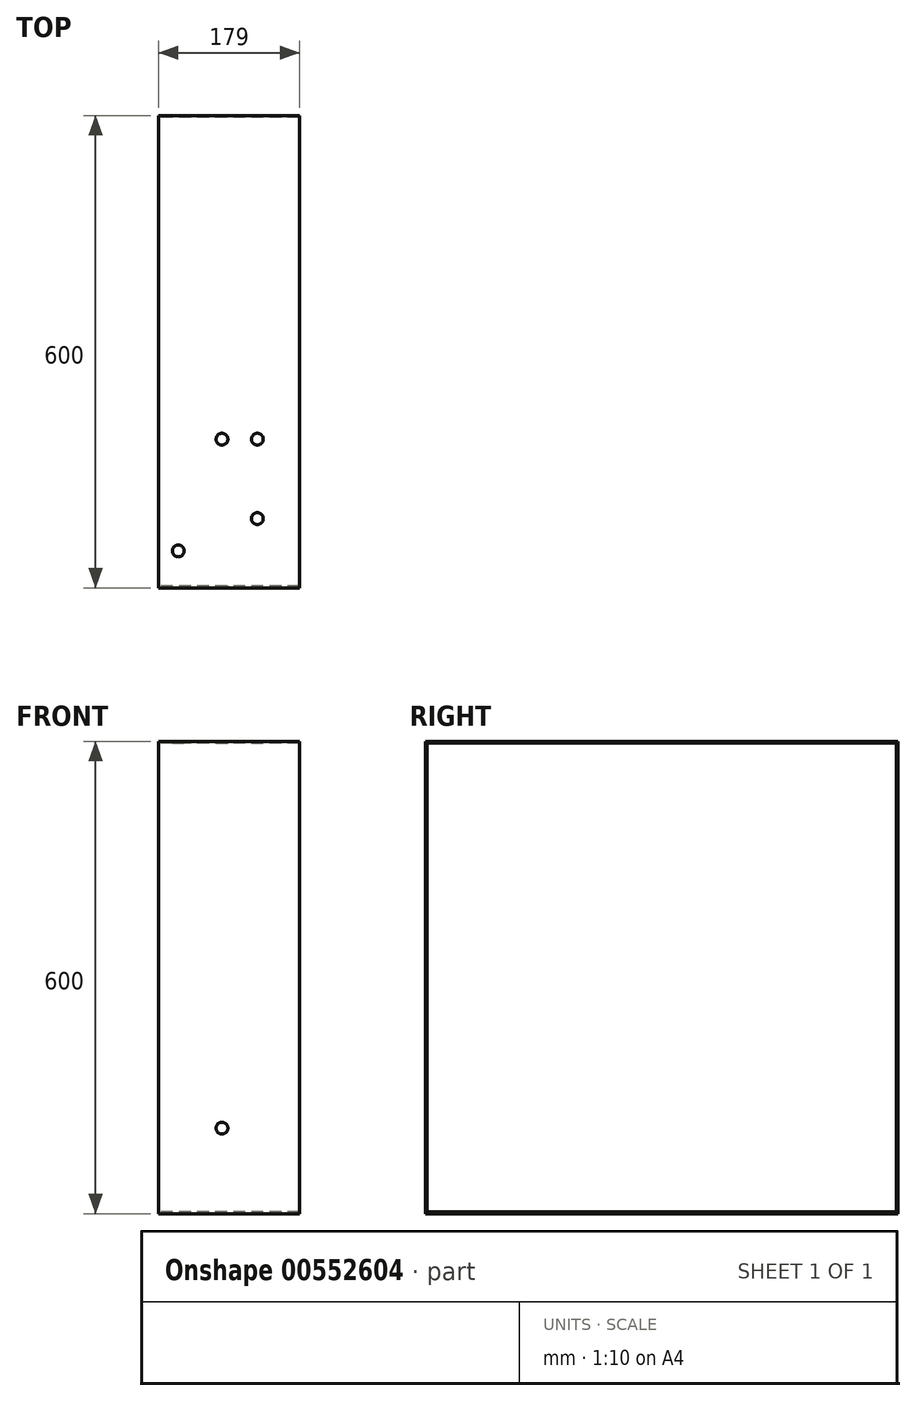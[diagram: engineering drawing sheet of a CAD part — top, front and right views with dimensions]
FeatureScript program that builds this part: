
annotation { "Feature Type Name" : "Feature", "Feature Type Description" : "" }
export const myFeature = defineFeature(function(context is Context, id is Id, definition is map)
    precondition{}
    {
        {
            var Q0;
            Q0=qCreatedBy(makeId("Right.planeOp"),FACE);
            var sketch = newSketch(context, id + "F0", { "sketchPlane" : qUnion([Q0])});
            skLineSegment(sketch, "E0", {"start": v(-190.86, -297.99) * mm, "end": v(405.14, -297.99) * mm});
            skLineSegment(sketch, "E1", {"start": v(-192.86, -299.99) * mm, "end": v(407.14, -299.99) * mm});
            skLineSegment(sketch, "E2", {"start": v(405.14, 298.01) * mm, "end": v(-190.86, 298.01) * mm});
            skLineSegment(sketch, "E3", {"start": v(407.14, 300.01) * mm, "end": v(-192.86, 300.01) * mm});
            skLineSegment(sketch, "E4", {"start": v(-192.86, 300.01) * mm, "end": v(-192.86, -299.99) * mm});
            skLineSegment(sketch, "E5", {"start": v(-190.86, 298.01) * mm, "end": v(-190.86, -297.99) * mm});
            skLineSegment(sketch, "E6", {"start": v(-139.36, -3.52) * mm, "end": v(-139.36, 3.48) * mm});
            skLineSegment(sketch, "E7", {"start": v(-146.36, 3.48) * mm, "end": v(-146.36, -3.52) * mm});
            skLineSegment(sketch, "E8", {"start": v(-139.36, 3.48) * mm, "end": v(-146.36, 3.48) * mm});
            skLineSegment(sketch, "E9", {"start": v(-146.36, -3.52) * mm, "end": v(-139.36, -3.52) * mm});
            skCircle(sketch, "E10", {"center": v(-142.86, -0.02) * mm, "radius": 16.5 * mm});
            skCircle(sketch, "E11", {"center": v(-142.86, -0.02) * mm, "radius": 8.5 * mm});
            skLineSegment(sketch, "E12", {"start": v(405.14, -297.99) * mm, "end": v(405.14, 298.01) * mm});
            skLineSegment(sketch, "E13", {"start": v(407.14, -299.99) * mm, "end": v(407.14, 300.01) * mm});
            skSolve(sketch);
        }
        {
            var Q0;
            Q0 = qSketchRegion(id + "F0", true);
            extrude(context, id + "F1", {"entities" : qUnion([Q0]), "depth" : 179 * mm, "offsetDistance" : 25 * mm});
        }
        {
            var Q0;
            Q0=makeQuery(id+"F1.opExtrude","SWEPT_FACE",FACE,{"disambiguationData":[OSD([sQuery(id+"F0.wireOp",EDGE,"E3")])]});
            var sketch = newSketch(context, id + "F2", { "sketchPlane" : qUnion([Q0])});
            skCircle(sketch, "E14", {"center": v(25, -145.96) * mm, "radius": 7.5 * mm});
            skCircle(sketch, "E15", {"center": v(80.5, -3.96) * mm, "radius": 7.5 * mm});
            skCircle(sketch, "E16", {"center": v(125.5, -3.96) * mm, "radius": 7.5 * mm});
            skCircle(sketch, "E17", {"center": v(125.5, -104.86) * mm, "radius": 7.5 * mm});
            skSolve(sketch);
        }
        {
            var Q0;
            Q0 = qSketchRegion(id + "F2", true);
            extrude(context, id + "F3", {"entities" : qUnion([Q0]), "operationType" : NewBodyOperationType.REMOVE, "oppositeDirection" : true, "depth" : 25 * mm, "offsetDistance" : 25 * mm});
        }
        {
            var Q0;
            Q0=makeQuery(id+"F1.opExtrude","SWEPT_FACE",FACE,{"disambiguationData":[OSD([sQuery(id+"F0.wireOp",EDGE,"E4")])]});
            var sketch = newSketch(context, id + "F4", { "sketchPlane" : qUnion([Q0])});
            skCircle(sketch, "E18", {"center": v(80.5, -191.29) * mm, "radius": 7.5 * mm});
            skSolve(sketch);
        }
        {
            var Q0;
            Q0 = qSketchRegion(id + "F4", true);
            extrude(context, id + "F5", {"entities" : qUnion([Q0]), "operationType" : NewBodyOperationType.REMOVE, "oppositeDirection" : true, "depth" : 25 * mm, "offsetDistance" : 25 * mm});
        }
    });
